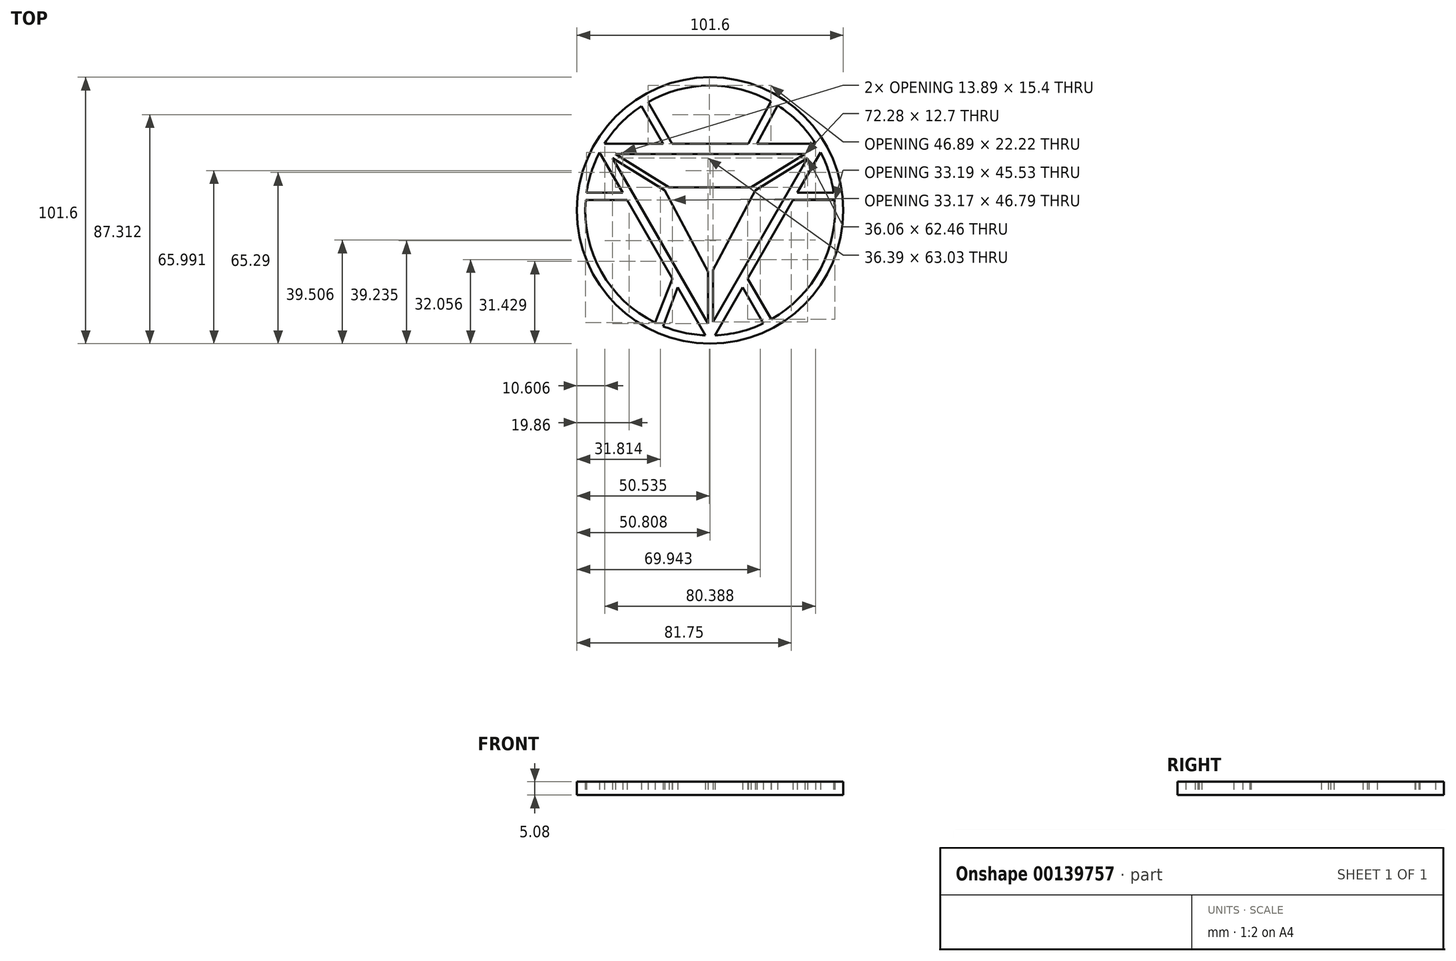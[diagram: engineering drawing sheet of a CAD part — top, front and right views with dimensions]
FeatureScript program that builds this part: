
annotation { "Feature Type Name" : "Feature", "Feature Type Description" : "" }
export const myFeature = defineFeature(function(context is Context, id is Id, definition is map)
    precondition{}
    {
        {
            var Q0;
            Q0=qCreatedBy(makeId("Top.planeOp"),FACE);
            var sketch = newSketch(context, id + "F0", { "sketchPlane" : qUnion([Q0])});
            skCircle(sketch, "E0", {"center": v(0, 0) * mm, "radius": 50.8 * mm});
            skLineSegment(sketch, "E1", {"start": v(-42.14, 22.19) * mm, "end": v(-33.25, 6.8) * mm});
            skPoint(sketch, "E1.startSnap0", {"position": v(-44, 6.8) * mm});
            skLineSegment(sketch, "E2", {"start": v(1.85, -47.59) * mm, "end": v(12.4, -29.31) * mm});
            skLineSegment(sketch, "E3", {"start": v(-40.29, 25.4) * mm, "end": v(-17.93, 25.4) * mm});
            skLineSegment(sketch, "E4", {"start": v(-36.13, 21.54) * mm, "end": v(36.15, 21.54) * mm});
            skLineSegment(sketch, "E5", {"start": v(37.17, 19.93) * mm, "end": v(1.11, -42.52) * mm});
            skLineSegment(sketch, "E6", {"start": v(-37.18, 19.95) * mm, "end": v(-0.8, -43.08) * mm});
            skLineSegment(sketch, "E7", {"start": v(-15.62, 8.84) * mm, "end": v(15.63, 8.84) * mm});
            skLineSegment(sketch, "E8", {"start": v(17.27, 7.62) * mm, "end": v(1.11, -22.7) * mm});
            skLineSegment(sketch, "E9", {"start": v(-0.8, -23.3) * mm, "end": v(-17.28, 7.63) * mm});
            skPoint(sketch, "E10.orphan", {"position": v(-37.64, 6.8) * mm});
            skPoint(sketch, "E11.start.orphan", {"position": v(-50.34, 6.8) * mm});
            skLineSegment(sketch, "E12", {"start": v(-47.14, 6.8) * mm, "end": v(-33.25, 6.8) * mm});
            skLineSegment(sketch, "E13", {"start": v(-47.45, 4.02) * mm, "end": v(-31.65, 4.02) * mm});
            skLineSegment(sketch, "E14", {"start": v(-12.4, -29.31) * mm, "end": v(-17.97, -44.1) * mm});
            skLineSegment(sketch, "E15", {"start": v(-14.36, -25.93) * mm, "end": v(-20.96, -42.76) * mm});
            skLineSegment(sketch, "E16", {"start": v(33.25, 6.8) * mm, "end": v(47.14, 6.8) * mm});
            skLineSegment(sketch, "E17", {"start": v(31.65, 4.02) * mm, "end": v(47.45, 4.02) * mm});
            skLineSegment(sketch, "E18", {"start": v(12.4, -29.31) * mm, "end": v(20.34, -43.06) * mm});
            skLineSegment(sketch, "E19", {"start": v(14.36, -25.93) * mm, "end": v(23.35, -41.5) * mm});
            skLineSegment(sketch, "E20", {"start": v(17.93, 25.4) * mm, "end": v(25.75, 40.07) * mm});
            skLineSegment(sketch, "E21", {"start": v(23.18, 41.6) * mm, "end": v(14.54, 25.4) * mm});
            skLineSegment(sketch, "E22", {"start": v(-17.93, 25.4) * mm, "end": v(-26.22, 39.76) * mm});
            skLineSegment(sketch, "E23", {"start": v(-23.7, 41.3) * mm, "end": v(-14.53, 25.4) * mm});
            skArc(sketch, "E24", {"start": v(40.29, 25.4) * mm, "mid": v(33.82, 33.53) * mm, "end": v(25.75, 40.07) * mm});
            skLineSegment(sketch, "E25", {"start": v(-37.18, 19.95) * mm, "end": v(-17.28, 7.63) * mm});
            skLineSegment(sketch, "E26", {"start": v(-36.13, 21.54) * mm, "end": v(-15.62, 8.84) * mm});
            skLineSegment(sketch, "E27", {"start": v(36.15, 21.54) * mm, "end": v(15.63, 8.84) * mm});
            skLineSegment(sketch, "E28", {"start": v(17.27, 7.62) * mm, "end": v(37.17, 19.93) * mm});
            skLineSegment(sketch, "E29", {"start": v(-0.8, -23.3) * mm, "end": v(-0.8, -43.08) * mm});
            skLineSegment(sketch, "E30", {"start": v(1.11, -22.7) * mm, "end": v(1.11, -42.52) * mm});
            skPoint(sketch, "E31.orphan", {"position": v(17.93, 8.84) * mm});
            skLineSegment(sketch, "E32.trimOffspring", {"start": v(17.93, 25.4) * mm, "end": v(40.29, 25.4) * mm});
            skArc(sketch, "E33.trimOffspring", {"start": v(47.14, 6.8) * mm, "mid": v(45.3, 14.7) * mm, "end": v(42.14, 22.19) * mm});
            skLineSegment(sketch, "E34.trimOffspring", {"start": v(33.25, 6.8) * mm, "end": v(42.14, 22.19) * mm});
            skLineSegment(sketch, "E35.trimOffspring", {"start": v(-31.65, 4.02) * mm, "end": v(-14.36, -25.93) * mm});
            skArc(sketch, "E36.trimOffspring", {"start": v(-47.45, 4.02) * mm, "mid": v(-41.44, -23.47) * mm, "end": v(-20.96, -42.76) * mm});
            skLineSegment(sketch, "E37.trimOffspring", {"start": v(-14.53, 25.4) * mm, "end": v(14.54, 25.4) * mm});
            skArc(sketch, "E38.trimOffspring", {"start": v(23.18, 41.6) * mm, "mid": v(-0.3, 47.62) * mm, "end": v(-23.7, 41.3) * mm});
            skArc(sketch, "E39.trimOffspring", {"start": v(-26.22, 39.76) * mm, "mid": v(-34.02, 33.33) * mm, "end": v(-40.29, 25.4) * mm});
            skPoint(sketch, "E40.orphan", {"position": v(-17.93, 8.84) * mm});
            skPoint(sketch, "E41.orphan", {"position": v(-44, 25.4) * mm});
            skArc(sketch, "E42.trimOffspring", {"start": v(-42.14, 22.19) * mm, "mid": v(-45.3, 14.7) * mm, "end": v(-47.14, 6.8) * mm});
            skPoint(sketch, "E43.orphan", {"position": v(0, -50.8) * mm});
            skArc(sketch, "E44.trimOffspring", {"start": v(1.85, -47.59) * mm, "mid": v(11.33, -46.26) * mm, "end": v(20.34, -43.06) * mm});
            skPoint(sketch, "E45.orphan", {"position": v(0, -44.45) * mm});
            skArc(sketch, "E46.trimOffspring", {"start": v(23.35, -41.5) * mm, "mid": v(42.09, -22.28) * mm, "end": v(47.45, 4.02) * mm});
            skLineSegment(sketch, "E47.trimOffspring", {"start": v(14.36, -25.93) * mm, "end": v(31.65, 4.02) * mm});
            skPoint(sketch, "E48.orphan", {"position": v(0, -24.78) * mm});
            skLineSegment(sketch, "E49.trimOffspring", {"start": v(-12.4, -29.31) * mm, "end": v(-1.85, -47.59) * mm});
            skArc(sketch, "E50.trimOffspring", {"start": v(-17.97, -44.1) * mm, "mid": v(-10.07, -46.55) * mm, "end": v(-1.85, -47.59) * mm});
            skSolve(sketch);
        }
        {
            var Q0;
            {var subQ0=sQuery(id+"F0.wireOp",EDGE,"E22");var subQ1=sQuery(id+"F0.wireOp",EDGE,"E0");var subQ2=makeQuery(id+"F0.imprint","INTERSECT",VERTEX,{"derivedFrom":[subQ1,subQ0]});Q0=makeQuery(id+"F0.imprint","IMPRINT",FACE,{"disambiguationData":[TD([[makeQuery(id+"F0.imprint","IMPRINT",EDGE,{"disambiguationData":[TD([[subQ2,1.0]])],"derivedFrom":subQ1}),1.0]])]});}
            var Q1;
            {var subQ0=sQuery(id+"F0.wireOp",EDGE,"E21");var subQ1=sQuery(id+"F0.wireOp",EDGE,"E0");var subQ2=makeQuery(id+"F0.imprint","INTERSECT",VERTEX,{"derivedFrom":[subQ1,subQ0]});Q1=makeQuery(id+"F0.imprint","IMPRINT",FACE,{"disambiguationData":[TD([[makeQuery(id+"F0.imprint","IMPRINT",EDGE,{"disambiguationData":[TD([[subQ2,-1.0]])],"derivedFrom":subQ1}),1.0]])]});}
            var Q2;
            {var subQ3=sQuery(id+"F0.wireOp",EDGE,"E25");Q2=makeQuery(id+"F0.imprint","IMPRINT",FACE,{"disambiguationData":[TD([[makeQuery(id+"F0.imprint","IMPRINT",EDGE,{"derivedFrom":subQ3}),1.0]])]});}
            var Q3;
            {var subQ3=sQuery(id+"F0.wireOp",EDGE,"E29");Q3=makeQuery(id+"F0.imprint","IMPRINT",FACE,{"disambiguationData":[TD([[makeQuery(id+"F0.imprint","IMPRINT",EDGE,{"derivedFrom":subQ3}),1.0]])]});}
            var Q4;
            {var subQ1=sQuery(id+"F0.wireOp",EDGE,"E7");var subQ6=sQuery(id+"F0.wireOp",EDGE,"E9");var subQ9=makeQuery(id+"F0.imprint","INTERSECT",VERTEX,{"derivedFrom":[subQ1,subQ6]});Q4=makeQuery(id+"F0.imprint","IMPRINT",FACE,{"disambiguationData":[TD([[makeQuery(id+"F0.imprint","IMPRINT",EDGE,{"disambiguationData":[TD([[subQ9,-1.0]])],"derivedFrom":subQ1}),-1.0]])]});}
            var Q5;
            {var subQ3=sQuery(id+"F0.wireOp",EDGE,"E27");Q5=makeQuery(id+"F0.imprint","IMPRINT",FACE,{"disambiguationData":[TD([[makeQuery(id+"F0.imprint","IMPRINT",EDGE,{"derivedFrom":subQ3}),1.0]])]});}
            var Q6;
            {var subQ19=sQuery(id+"F0.wireOp",EDGE,"E1");var subQ25=makeQuery(id+"F0.imprint","INTERSECT",VERTEX,{"derivedFrom":[subQ19,sQuery(id+"F0.wireOp",EDGE,"E12")]});Q6=makeQuery(id+"F0.imprint","IMPRINT",FACE,{"disambiguationData":[TD([[makeQuery(id+"F0.imprint","IMPRINT",EDGE,{"disambiguationData":[TD([[subQ25,1.0]])],"derivedFrom":subQ19}),1.0]])]});}
            var Q7;
            {var subQ1=sQuery(id+"F0.wireOp",EDGE,"E2");var subQ3=sQuery(id+"F0.wireOp",EDGE,"E24");var subQ4=makeQuery(id+"F0.imprint","INTERSECT",VERTEX,{"disambiguationData":[OD(1.0)],"derivedFrom":[subQ1,subQ3]});Q7=makeQuery(id+"F0.imprint","IMPRINT",FACE,{"disambiguationData":[TD([[makeQuery(id+"F0.imprint","IMPRINT",EDGE,{"disambiguationData":[TD([[subQ4,-1.0]])],"derivedFrom":subQ3}),-1.0]])]});}
            var Q8;
            {var subQ0=sQuery(id+"F0.wireOp",EDGE,"E20");var subQ1=sQuery(id+"F0.wireOp",EDGE,"E0");var subQ2=makeQuery(id+"F0.imprint","INTERSECT",VERTEX,{"derivedFrom":[subQ1,subQ0]});Q8=makeQuery(id+"F0.imprint","IMPRINT",FACE,{"disambiguationData":[TD([[makeQuery(id+"F0.imprint","IMPRINT",EDGE,{"disambiguationData":[TD([[subQ2,-1.0]])],"derivedFrom":subQ1}),1.0]])]});}
            var Q9;
            {var subQ0=sQuery(id+"F0.wireOp",EDGE,"E16");var subQ1=sQuery(id+"F0.wireOp",EDGE,"E0");var subQ2=makeQuery(id+"F0.imprint","INTERSECT",VERTEX,{"derivedFrom":[subQ1,subQ0]});Q9=makeQuery(id+"F0.imprint","IMPRINT",FACE,{"disambiguationData":[TD([[makeQuery(id+"F0.imprint","IMPRINT",EDGE,{"disambiguationData":[TD([[subQ2,1.0]])],"derivedFrom":subQ1}),1.0]])]});}
            var Q10;
            {var subQ0=sQuery(id+"F0.wireOp",EDGE,"E17");var subQ1=sQuery(id+"F0.wireOp",EDGE,"E0");var subQ2=makeQuery(id+"F0.imprint","INTERSECT",VERTEX,{"derivedFrom":[subQ1,subQ0]});Q10=makeQuery(id+"F0.imprint","IMPRINT",FACE,{"disambiguationData":[TD([[makeQuery(id+"F0.imprint","IMPRINT",EDGE,{"disambiguationData":[TD([[subQ2,1.0]])],"derivedFrom":subQ1}),1.0]])]});}
            var Q11;
            {var subQ0=sQuery(id+"F0.wireOp",EDGE,"E18");var subQ1=sQuery(id+"F0.wireOp",EDGE,"E0");var subQ2=makeQuery(id+"F0.imprint","INTERSECT",VERTEX,{"derivedFrom":[subQ1,subQ0]});Q11=makeQuery(id+"F0.imprint","IMPRINT",FACE,{"disambiguationData":[TD([[makeQuery(id+"F0.imprint","IMPRINT",EDGE,{"disambiguationData":[TD([[subQ2,-1.0]])],"derivedFrom":subQ1}),1.0]])]});}
            var Q12;
            {var subQ1=sQuery(id+"F0.wireOp",EDGE,"E1");var subQ3=sQuery(id+"F0.wireOp",EDGE,"E24");var subQ4=makeQuery(id+"F0.imprint","INTERSECT",VERTEX,{"disambiguationData":[OD(1.0)],"derivedFrom":[subQ1,subQ3]});Q12=makeQuery(id+"F0.imprint","IMPRINT",FACE,{"disambiguationData":[TD([[makeQuery(id+"F0.imprint","IMPRINT",EDGE,{"disambiguationData":[TD([[subQ4,-1.0]])],"derivedFrom":subQ3}),-1.0]])]});}
            var Q13;
            {var subQ0=sQuery(id+"F0.wireOp",EDGE,"E14");var subQ1=sQuery(id+"F0.wireOp",EDGE,"E0");var subQ2=makeQuery(id+"F0.imprint","INTERSECT",VERTEX,{"derivedFrom":[subQ1,subQ0]});Q13=makeQuery(id+"F0.imprint","IMPRINT",FACE,{"disambiguationData":[TD([[makeQuery(id+"F0.imprint","IMPRINT",EDGE,{"disambiguationData":[TD([[subQ2,1.0]])],"derivedFrom":subQ1}),1.0]])]});}
            var Q14;
            {var subQ0=sQuery(id+"F0.wireOp",EDGE,"E13");var subQ1=sQuery(id+"F0.wireOp",EDGE,"E0");var subQ2=makeQuery(id+"F0.imprint","INTERSECT",VERTEX,{"derivedFrom":[subQ1,subQ0]});Q14=makeQuery(id+"F0.imprint","IMPRINT",FACE,{"disambiguationData":[TD([[makeQuery(id+"F0.imprint","IMPRINT",EDGE,{"disambiguationData":[TD([[subQ2,-1.0]])],"derivedFrom":subQ1}),1.0]])]});}
            var Q15;
            {var subQ1=sQuery(id+"F0.wireOp",EDGE,"E1");var subQ3=sQuery(id+"F0.wireOp",EDGE,"E24");var subQ4=makeQuery(id+"F0.imprint","INTERSECT",VERTEX,{"disambiguationData":[OD(0.0)],"derivedFrom":[subQ1,subQ3]});Q15=makeQuery(id+"F0.imprint","IMPRINT",FACE,{"disambiguationData":[TD([[makeQuery(id+"F0.imprint","IMPRINT",EDGE,{"disambiguationData":[TD([[subQ4,1.0]])],"derivedFrom":subQ3}),-1.0]])]});}
            var Q16;
            {var subQ0=sQuery(id+"F0.wireOp",EDGE,"E12");var subQ1=sQuery(id+"F0.wireOp",EDGE,"E0");var subQ2=makeQuery(id+"F0.imprint","INTERSECT",VERTEX,{"derivedFrom":[subQ1,subQ0]});Q16=makeQuery(id+"F0.imprint","IMPRINT",FACE,{"disambiguationData":[TD([[makeQuery(id+"F0.imprint","IMPRINT",EDGE,{"disambiguationData":[TD([[subQ2,-1.0]])],"derivedFrom":subQ1}),1.0]])]});}
            extrude(context, id + "F1", {"entities" : qUnion([Q0, Q1, Q2, Q3, Q4, Q5, Q6, Q7, Q8, Q9, Q10, Q11, Q12, Q13, Q14, Q15, Q16]), "depth" : 5.08 * mm});
        }
    });
